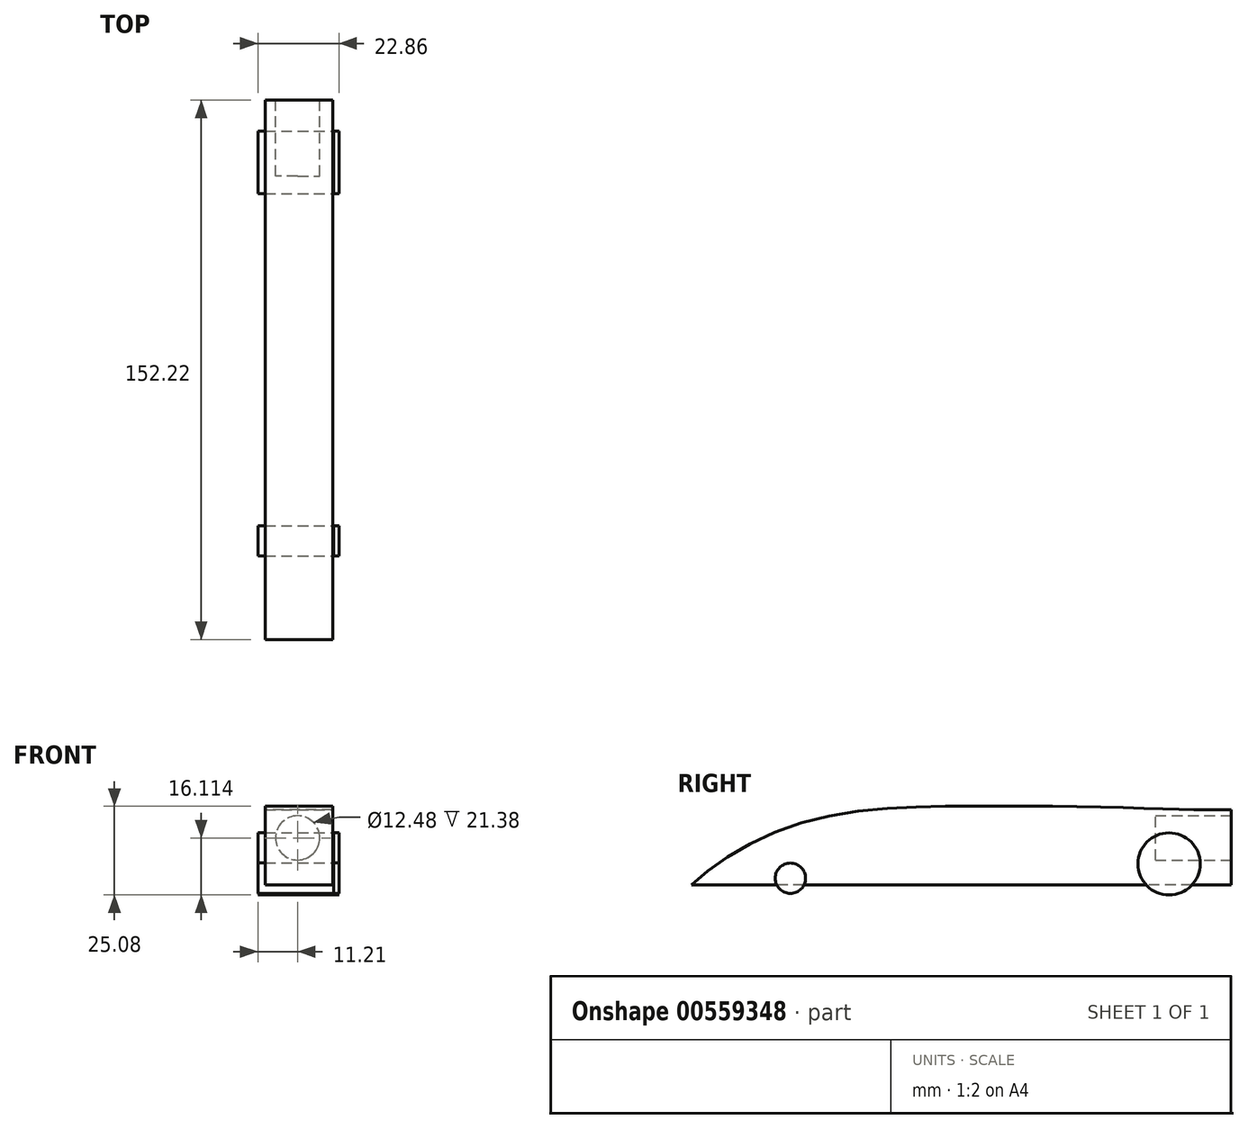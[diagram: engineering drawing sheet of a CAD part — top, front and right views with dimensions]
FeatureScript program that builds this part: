
annotation { "Feature Type Name" : "Feature", "Feature Type Description" : "" }
export const myFeature = defineFeature(function(context is Context, id is Id, definition is map)
    precondition{}
    {
        {
            var Q0;
            Q0=qCreatedBy(makeId("Right.planeOp"),FACE);
            var sketch = newSketch(context, id + "F0", { "sketchPlane" : qUnion([Q0])});
            skFitSpline(sketch, "E0", {"points": [v(-76.23, 0) * mm, v(-45.72, 17.38) * mm, v(0, 22.19) * mm, v(36.78, 22) * mm, v(59.72, 21.36) * mm, v(76, 21.17) * mm], "startDerivative": vector(92.72, 88.4) * mm, "endDerivative": vector(158.73, 1.04) * mm});
            skLineSegment(sketch, "E1", {"start": v(76, 21.17) * mm, "end": v(76, 0) * mm});
            skLineSegment(sketch, "E2", {"start": v(76, 0) * mm, "end": v(-76.23, 0) * mm});
            skSolve(sketch);
        }
        {
            var Q0;
            Q0 = qSketchRegion(id + "F0", true);
            extrude(context, id + "F1", {"entities" : qUnion([Q0]), "depth" : 19.05 * mm, "offsetDistance" : 25.4 * mm});
        }
        {
            var Q0;
            Q0=qCreatedBy(makeId("Front.planeOp"),FACE);
            cPlane(context, id + "F2", {"entities" : qUnion([Q0]), "cplaneType" : CPlaneType.OFFSET, "offset" : 85.6 * mm, "oppositeDirection" : true, "width" : 152.4 * mm, "height" : 152.4 * mm});
        }
        {
            var Q0;
            Q0=qCreatedBy(id+"F2.planeOp",FACE);
            var sketch = newSketch(context, id + "F3", { "sketchPlane" : qUnion([Q0])});
            skCircle(sketch, "E3", {"center": v(9.18, 13.25) * mm, "radius": 6.24 * mm});
            skSolve(sketch);
        }
        {
            var Q0;
            Q0=makeQuery(id+"F3.imprint","IMPRINT",FACE,{"disambiguationData":[TD([[makeQuery(id+"F3.imprint","IMPRINT",EDGE,{"derivedFrom":sQuery(id+"F3.wireOp",EDGE,"E3")}),1.0]])]});
            extrude(context, id + "F4", {"entities" : qUnion([Q0]), "operationType" : NewBodyOperationType.REMOVE, "depth" : 30.99 * mm, "offsetDistance" : 25.4 * mm});
        }
        {
            var Q0;
            Q0=qCreatedBy(makeId("Right.planeOp"),FACE);
            cPlane(context, id + "F5", {"entities" : qUnion([Q0]), "cplaneType" : CPlaneType.OFFSET, "offset" : 19.3 * mm, "width" : 152.4 * mm, "height" : 152.4 * mm});
        }
        {
            var Q0;
            Q0=qCreatedBy(id+"F5.planeOp",FACE);
            var sketch = newSketch(context, id + "F6", { "sketchPlane" : qUnion([Q0])});
            skCircle(sketch, "E4", {"center": v(-48.4, 1.86) * mm, "radius": 4.28 * mm});
            skCircle(sketch, "E5", {"center": v(58.44, 5.92) * mm, "radius": 8.77 * mm});
            skSolve(sketch);
        }
        {
            var Q0;
            Q0 = qSketchRegion(id + "F6", true);
            extrude(context, id + "F7", {"entities" : qUnion([Q0]), "depth" : 1.52 * mm, "offsetDistance" : 25.4 * mm});
        }
        {
            var Q0;
            Q0=makeQuery(id+"F7.opExtrude","CAP_FACE",FACE,{"disambiguationData":[OSD([sQuery(id+"F6.wireOp",EDGE,"E4")])],"isStart":false});
            var Q1;
            Q1=makeQuery(id+"F7.opExtrude","CAP_FACE",FACE,{"disambiguationData":[OSD([sQuery(id+"F6.wireOp",EDGE,"E5")])],"isStart":false});
            extrude(context, id + "F8", {"entities" : qUnion([Q0, Q1]), "oppositeDirection" : true, "depth" : 22.86 * mm, "offsetDistance" : 25.4 * mm});
        }
    });
